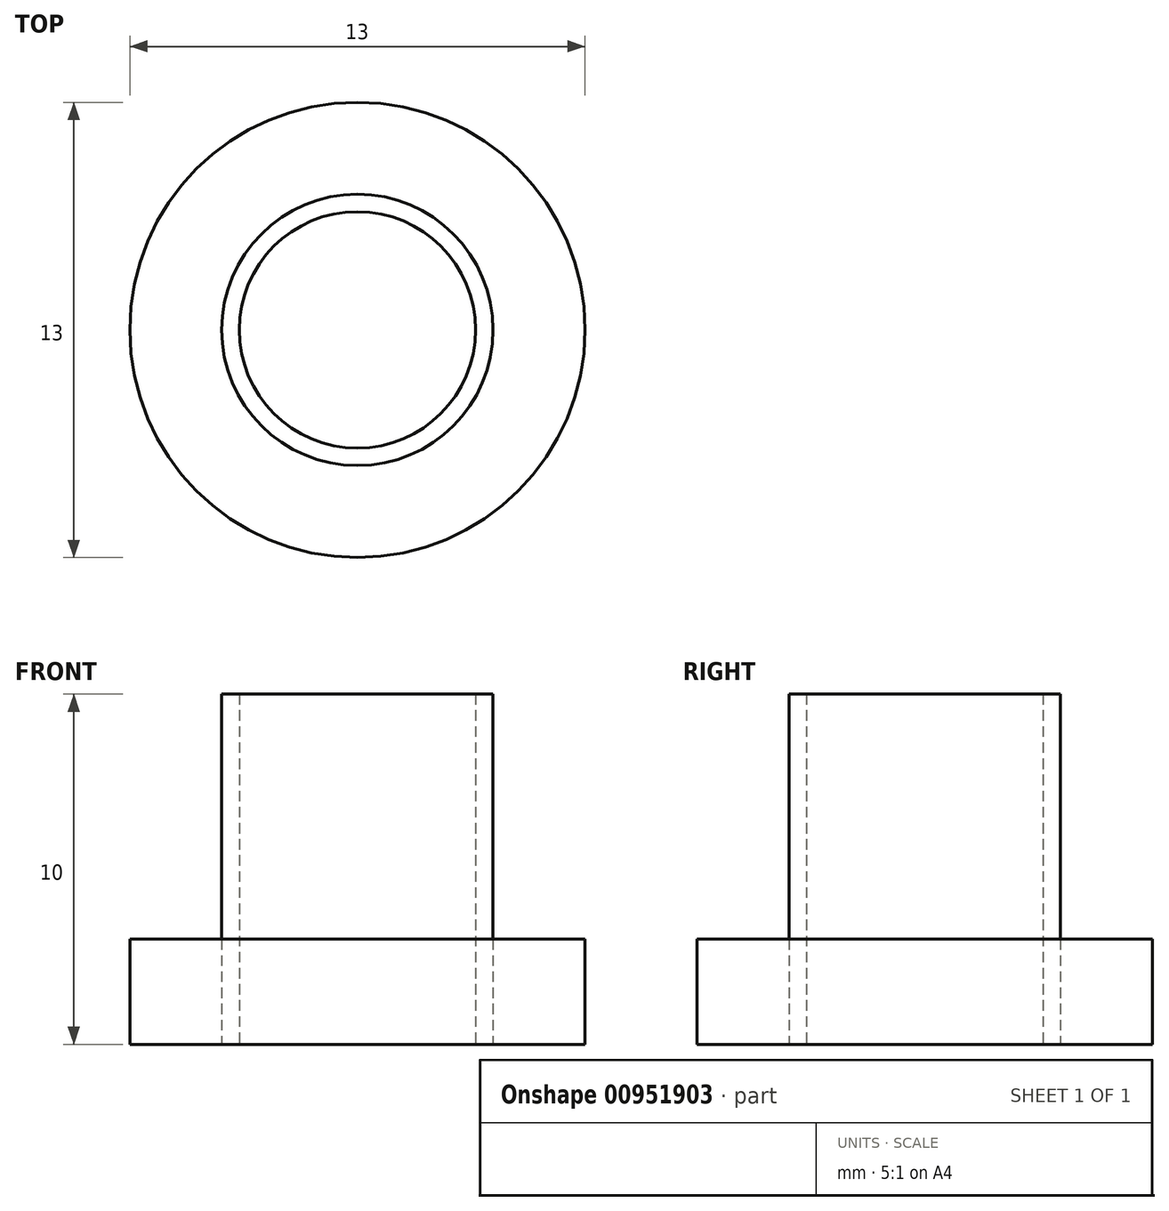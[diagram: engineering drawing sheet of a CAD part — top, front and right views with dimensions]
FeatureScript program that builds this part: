
annotation { "Feature Type Name" : "Feature", "Feature Type Description" : "" }
export const myFeature = defineFeature(function(context is Context, id is Id, definition is map)
    precondition{}
    {
        {
            var Q0;
            Q0=qCreatedBy(makeId("Top.planeOp"),FACE);
            var sketch = newSketch(context, id + "F0", { "sketchPlane" : qUnion([Q0])});
            skCircle(sketch, "E0", {"center": v(-9.5, 0) * mm, "radius": 3.88 * mm});
            skCircle(sketch, "E1", {"center": v(-9.5, 0) * mm, "radius": 6.5 * mm});
            skCircle(sketch, "E2", {"center": v(-9.5, 0) * mm, "radius": 3.38 * mm});
            skPoint(sketch, "E3.center.orphan", {"position": v(-39.15, 0) * mm});
            skSolve(sketch);
        }
        {
            var Q0;
            Q0=makeQuery(id+"F0.imprint","IMPRINT",FACE,{"disambiguationData":[TD([[makeQuery(id+"F0.imprint","IMPRINT",EDGE,{"derivedFrom":sQuery(id+"F0.wireOp",EDGE,"OktzW2Pz-47kU-gWwa-kMjT-OYjADVK3GVA4")}),1.0]])]});
            var Q1;
            Q1=makeQuery(id+"F0.imprint","IMPRINT",FACE,{"disambiguationData":[TD([[makeQuery(id+"F0.imprint","IMPRINT",EDGE,{"derivedFrom":sQuery(id+"F0.wireOp",EDGE,"E0")}),-1.0]])]});
            extrude(context, id + "F1", {"entities" : qUnion([Q0, Q1]), "depth" : 3 * mm, "offsetDistance" : 25 * mm});
        }
        {
            var Q0;
            Q0=makeQuery(id+"F0.imprint","IMPRINT",FACE,{"disambiguationData":[TD([[makeQuery(id+"F0.imprint","IMPRINT",EDGE,{"derivedFrom":sQuery(id+"F0.wireOp",EDGE,"E0")}),1.0]])]});
            extrude(context, id + "F2", {"entities" : qUnion([Q0]), "depth" : 10 * mm, "offsetDistance" : 25 * mm});
        }
    });
